# Revit family: Iiris 18W
name_source: partatom
category: Lighting Fixtures
units: mm (PartAtom-declared; Revit-internal decimal feet)

## family parameters
Cut with Voids When Loaded = No
Host = Face
Light Source = Yes
OmniClass Number = 23.80.70.11.11
OmniClass Title = General Luminaries, Non Directional
Part Type = Normal
Room Calculation Point = No
Round Connector Dimension = Use Diameter
Shared = No

## types (24) — shared parameters
Beam Angle = 90°
CRI = 85
Color Filter = 16777215
Cutout = 150mm
Default Elevation = 1219 mm
Depth = 60mm
Description = Downlight
Dimensions = 170mm x 45mm
Dimmable = Yes
Dimming Lamp Color Temperature Shift = <None>
Directivity = No
Driver = Separate
Housing Material = Aluminium
IP Code = IP44
Lamp = LED
Last Updated = 25.2.2016
Lifetime L70 = 40000h
Manufacturer = Winled Oy Ltd
Model = Iiris 18W
Operating Temperature Range = -20° to +40°C
Tilt Angle = -90.00°
Type Image = Iiris 18W.png
URL = www.winled.fi
Wattage Comments = 18W

## per-type parameters (varying)
| type | Casing Color | Color | Color Temperature | Lumens Output | Photometric Web File | Product Number | Voltage |
| Iiris 18W, Neutral White, Brushed Aluminium, 110V - 34XAV998N018X | Brushed Aluminium | Brushed Aluminium | 4000K | 1427lm | Iiris 18W NV.ies | 34XAV998N018X | 110 V |
| Iiris 18W, Neutral White, Brushed Aluminium, 0-10V, 110V - 34XAV998N018X10 | Brushed Aluminium | Brushed Aluminium | 4000K | 1427lm | Iiris 18W NV.ies | 34XAV998N018X10 | 110 V |
| Iiris 18W, Neutral White, Brushed Aluminium, Dali, 110V - 34XAV998N018XDA | Brushed Aluminium | Brushed Aluminium | 4000K | 1427lm | Iiris 18W NV.ies | 34XAV998N018XDA | 110 V |
| Iiris 18W, Neutral White, White, 110V - 34XAV996N018X | White | White Metal | 4000K | 1427lm | Iiris 18W NV.ies | 34XAV996N018X | 110 V |
| Iiris 18W, Neutral White, White, 0-10V, 110V - 34XAV996N018X10 | White | White Metal | 4000K | 1427lm | Iiris 18W NV.ies | 34XAV996N018X10 | 110 V |
| Iiris 18W, Neutral White, White, Dali, 110V - 34XAV996N018XDA | White | White Metal | 4000K | 1427lm | Iiris 18W NV.ies | 34XAV996N018XDA | 110 V |
| Iiris 18W, Warm White, White, 110V - 34XAV996L018X | White | White Metal | 3000K | 1398lm | Iiris 18W LV.ies | 34XAV996L018X | 110 V |
| Iiris 18W, Warm White, White, 0-10V, 110V - 34XAV996L018X10 | White | White Metal | 3000K | 1398lm | Iiris 18W LV.ies | 34XAV996L018X10 | 110 V |
| Iiris 18W, Warm White, White, Dali, 110V - 34XAV996L018XDA | White | White Metal | 3000K | 1398lm | Iiris 18W LV.ies | 34XAV996L018XDA | 110 V |
| Iiris 18W, Warm White, Brushed Aluminium, 110V - 34XAV998L018X | Brushed Aluminium | Brushed Aluminium | 3000K | 1398lm | Iiris 18W LV.ies | 34XAV998L018X | 110 V |
| Iiris 18W, Warm White, Brushed Aluminium, 0-10V, 110V - 34XAV998L018X10 | Brushed Aluminium | Brushed Aluminium | 3000K | 1398lm | Iiris 18W LV.ies | 34XAV998L018X10 | 110 V |
| Iiris 18W, Warm White, Brushed Aluminium, Dali, 110V - 34XAV998L018XDA | Brushed Aluminium | Brushed Aluminium | 3000K | 1398lm | Iiris 18W LV.ies | 34XAV998L018XDA | 110 V |
| Iiris 18W, Neutral White, Brushed Aluminium, 0-10V, 230V - 34AV998N018X10 | Brushed Aluminium | Brushed Aluminium | 4000K | 1427lm | Iiris 18W NV.ies | 34AV998N018X10 | 230 V |
| Iiris 18W, Neutral White, Brushed Aluminium, 230V - 34AV998N018X | Brushed Aluminium | Brushed Aluminium | 4000K | 1427lm | Iiris 18W NV.ies | 34AV998N018X | 230 V |
| Iiris 18W, Neutral White, Brushed Aluminium, Dali, 230V - 34AV998N018XDA | Brushed Aluminium | Brushed Aluminium | 4000K | 1427lm | Iiris 18W NV.ies | 34AV998N018XDA | 230 V |
| Iiris 18W, Neutral White, White, 0-10V, 230V - 34AV996N018X10 | White | White Metal | 4000K | 1427lm | Iiris 18W NV.ies | 34AV996N018X10 | 230 V |
| Iiris 18W, Neutral White, White, 230V - 34AV996N018X | White | White Metal | 4000K | 1427lm | Iiris 18W NV.ies | 34AV996N018X | 230 V |
| Iiris 18W, Neutral White, White, Dali, 230V - 34AV996N018XDA | White | White Metal | 4000K | 1427lm | Iiris 18W NV.ies | 34AV996N018XDA | 230 V |
| Iiris 18W, Warm White, Brushed Aluminium, 0-10V, 230V - 34AV998L018X10 | Brushed Aluminium | Brushed Aluminium | 3000K | 1398lm | Iiris 18W LV.ies | 34AV998L018X10 | 230 V |
| Iiris 18W, Warm White, Brushed Aluminium, 230V - 34AV998L018X | Brushed Aluminium | Brushed Aluminium | 3000K | 1398lm | Iiris 18W LV.ies | 34AV998L018X | 230 V |
| Iiris 18W, Warm White, Brushed Aluminium, Dali, 230V - 34AV998L018XDA | Brushed Aluminium | Brushed Aluminium | 3000K | 1398lm | Iiris 18W LV.ies | 34AV998L018XDA | 230 V |
| Iiris 18W, Warm White, White, 0-10V, 230V - 34AV996L018X10 | White | White Metal | 3000K | 1398lm | Iiris 18W LV.ies | 34AV996L018X10 | 230 V |
| Iiris 18W, Warm White, White, 230V - 34AV996L018X | White | White Metal | 3000K | 1398lm | Iiris 18W LV.ies | 34AV996L018X | 230 V |
| Iiris 18W, Warm White, White, Dali, 230V - 34AV996L018XDA | White | White Metal | 3000K | 1398lm | Iiris 18W LV.ies | 34AV996L018XDA | 230 V |

## geometry (parser evidence)
native form markers: Sweep x4
no freeform markers — native parametric forms only
